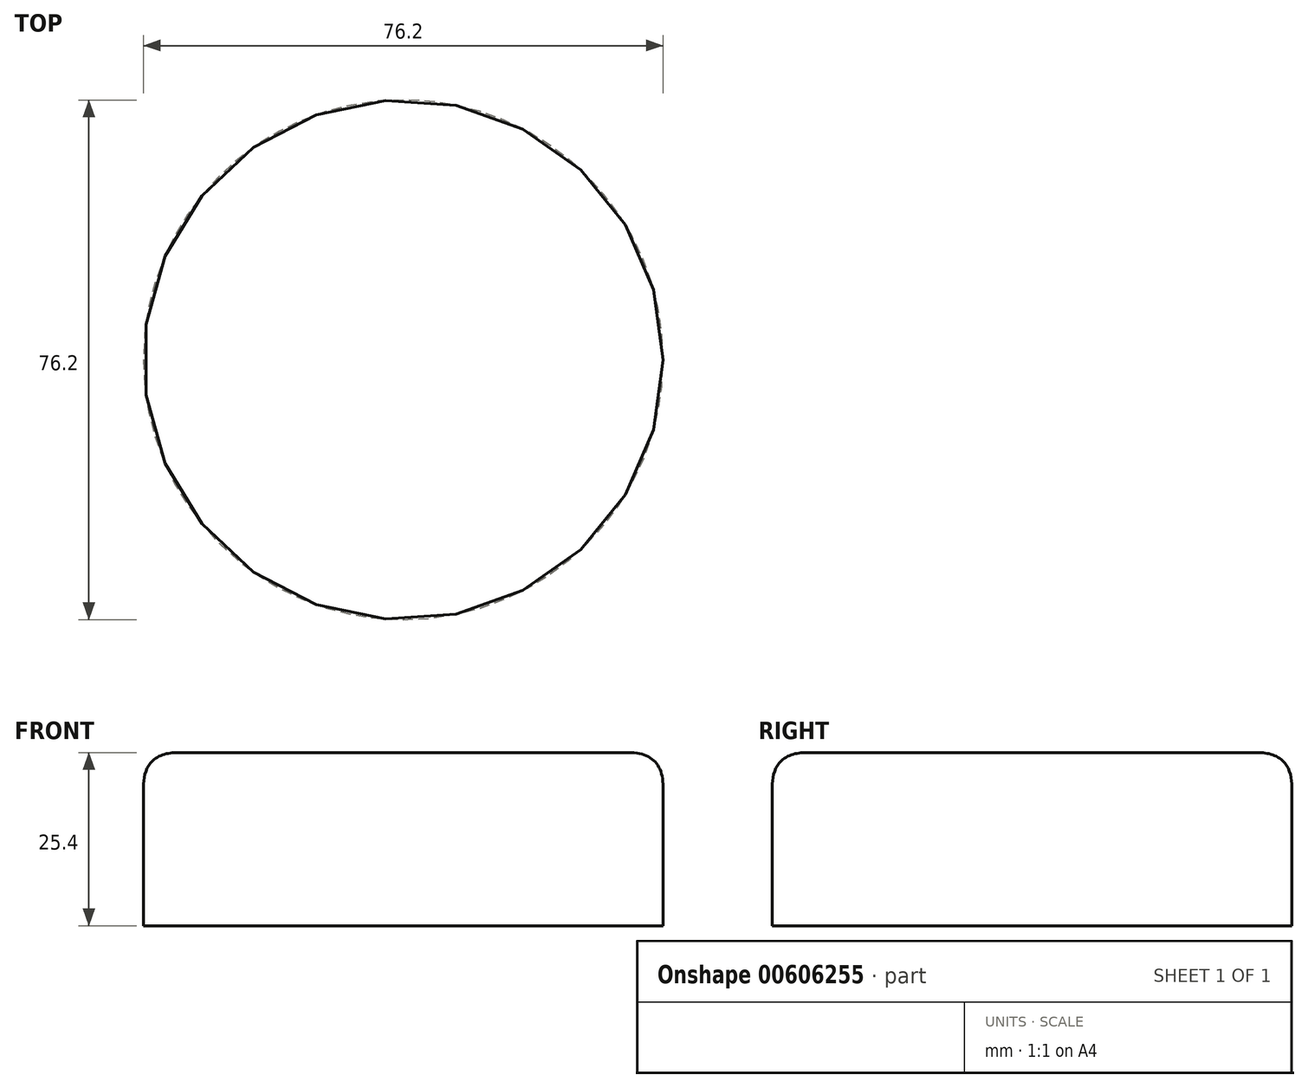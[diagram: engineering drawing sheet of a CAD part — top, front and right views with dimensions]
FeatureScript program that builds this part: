
annotation { "Feature Type Name" : "Feature", "Feature Type Description" : "" }
export const myFeature = defineFeature(function(context is Context, id is Id, definition is map)
    precondition{}
    {
        {
            var Q0;
            Q0=qCreatedBy(makeId("Top.planeOp"),FACE);
            var sketch = newSketch(context, id + "F0", { "sketchPlane" : qUnion([Q0])});
            skCircle(sketch, "E0", {"center": v(0, 0) * mm, "radius": 38.1 * mm});
            skPoint(sketch, "E1", {"position": v(-10.01, 36.76) * mm});
            skSolve(sketch);
        }
        {
            var Q0;
            Q0=makeQuery(id+"F0.imprint","IMPRINT",FACE,{"disambiguationData":[TD([[makeQuery(id+"F0.imprint","IMPRINT",EDGE,{"derivedFrom":sQuery(id+"F0.wireOp",EDGE,"E0")}),1.0]])]});
            extrude(context, id + "F1", {"entities" : qUnion([Q0]), "depth" : 25.4 * mm, "offsetDistance" : 25.4 * mm});
        }
        {
            var Q0;
            Q0=makeQuery(id+"F1.opExtrude","CAP_FACE",FACE,{"disambiguationData":[OSD([sQuery(id+"F0.wireOp",EDGE,"E0")])],"isStart":false});
            fillet(context, id + "F2", {"entities" : qUnion([Q0]), "radius" : 5.08 * mm, "tangentPropagation" : true, "rho" : 0.5, "crossSection" : FilletCrossSection.CONIC, "allowEdgeOverflow" : false});
        }
    });
